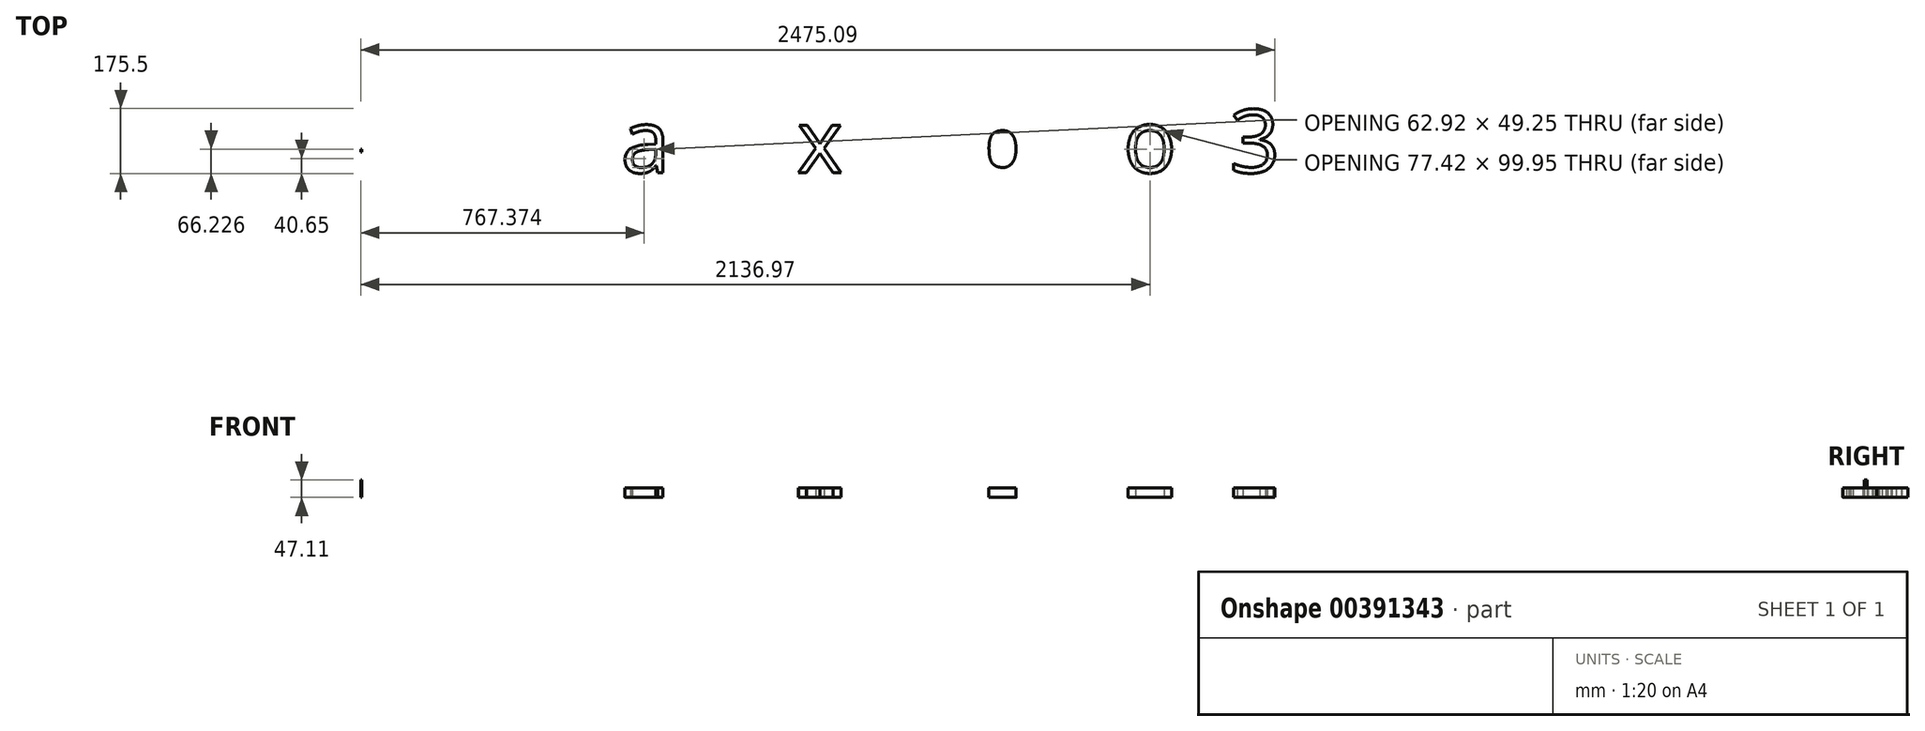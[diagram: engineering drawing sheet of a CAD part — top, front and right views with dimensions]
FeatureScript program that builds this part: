
annotation { "Feature Type Name" : "Feature", "Feature Type Description" : "" }
export const myFeature = defineFeature(function(context is Context, id is Id, definition is map)
    precondition{}
    {
        {
            var Q0;
            Q0=qCreatedBy(makeId("Right.planeOp"),FACE);
            var sketch = newSketch(context, id + "F0", { "sketchPlane" : qUnion([Q0])});
            skLineSegment(sketch, "E0.bottom", {"start": v(-34.55, 47.11) * mm, "end": v(-42.35, 47.11) * mm});
            skLineSegment(sketch, "E0.top", {"start": v(-34.55, 0) * mm, "end": v(-42.35, 0) * mm});
            skLineSegment(sketch, "E0.left", {"start": v(-34.55, 47.11) * mm, "end": v(-34.55, 0) * mm});
            skLineSegment(sketch, "E0.right", {"start": v(-42.35, 47.11) * mm, "end": v(-42.35, 0) * mm});
            skSolve(sketch);
        }
        {
            var Q0;
            Q0 = qSketchRegion(id + "F0", true);
            extrude(context, id + "F1", {"entities" : qUnion([Q0]), "depth" : 2.54 * mm});
        }
        {
            var Q0;
            Q0=qCreatedBy(makeId("Top.planeOp"),FACE);
            var sketch = newSketch(context, id + "F2", { "sketchPlane" : qUnion([Q0])});
            skText(sketch, "E1", { "text": "this is an example of 3d text creation", "fontName": "OpenSans-Regular.ttf"});
            const initialGuessF2  = {"E1": [0, -0.09808, 1, 0, 0.17218]};
            skSetInitialGuess(sketch, initialGuessF2);
            skSolve(sketch);
        }
        {
            var Q0;
            Q0=makeQuery(id+"F2.imprint","IMPRINT",FACE,{"disambiguationData":[TD([[makeQuery(id+"F2.imprint","IMPRINT",EDGE,{"derivedFrom":sQuery(id+"F2.wireOp",EDGE,"E1.sketch_text.stroke-111")}),-1.0]])]});
            var Q1;
            Q1=makeQuery(id+"F2.imprint","IMPRINT",FACE,{"disambiguationData":[TD([[makeQuery(id+"F2.imprint","IMPRINT",EDGE,{"derivedFrom":sQuery(id+"F2.wireOp",EDGE,"E1.sketch_text.stroke-174")}),-1.0]])]});
            var Q2;
            Q2=makeQuery(id+"F2.imprint","IMPRINT",FACE,{"disambiguationData":[TD([[makeQuery(id+"F2.imprint","IMPRINT",EDGE,{"derivedFrom":sQuery(id+"F2.wireOp",EDGE,"E1.sketch_text.stroke-257")}),1.0]])]});
            var Q3;
            Q3=makeQuery(id+"F2.imprint","IMPRINT",FACE,{"disambiguationData":[TD([[makeQuery(id+"F2.imprint","IMPRINT",EDGE,{"derivedFrom":sQuery(id+"F2.wireOp",EDGE,"E1.sketch_text.stroke-289")}),-1.0]])]});
            var Q4;
            Q4=makeQuery(id+"F2.imprint","IMPRINT",FACE,{"disambiguationData":[TD([[makeQuery(id+"F2.imprint","IMPRINT",EDGE,{"derivedFrom":sQuery(id+"F2.wireOp",EDGE,"E1.sketch_text.stroke-323")}),-1.0]])]});
            extrude(context, id + "F3", {"entities" : qUnion([Q0, Q1, Q2, Q3, Q4]), "depth" : 25.4 * mm});
        }
    });
